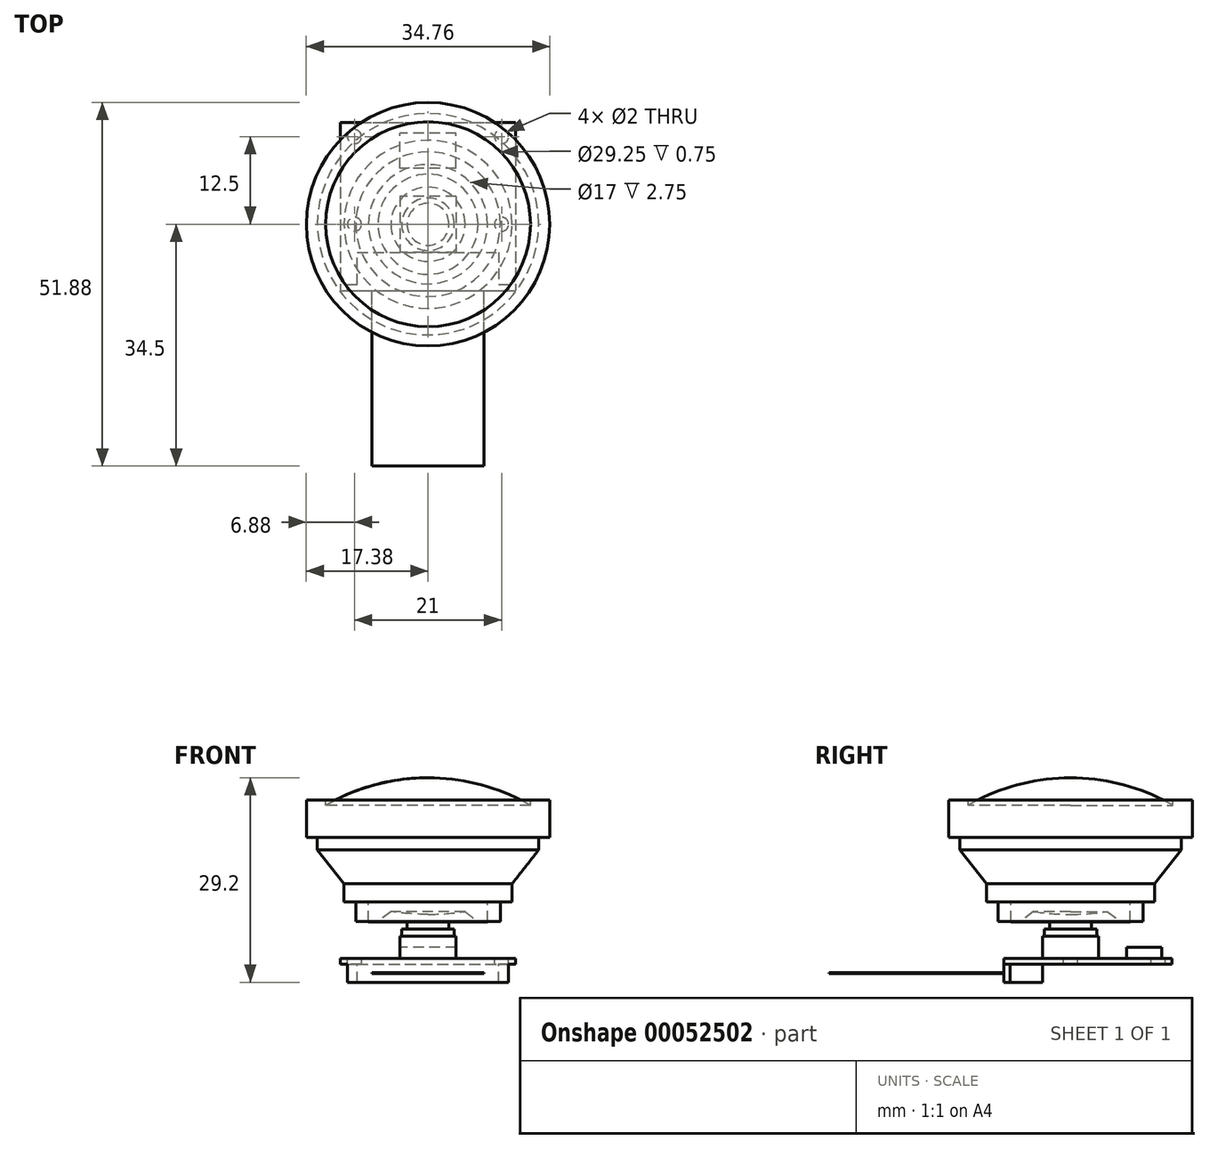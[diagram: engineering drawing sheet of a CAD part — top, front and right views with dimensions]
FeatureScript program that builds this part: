
annotation { "Feature Type Name" : "Feature", "Feature Type Description" : "" }
export const myFeature = defineFeature(function(context is Context, id is Id, definition is map)
    precondition{}
    {
        {
            var Q0;
            Q0=qCreatedBy(makeId("Top.planeOp"),FACE);
            var sketch = newSketch(context, id + "F0", { "sketchPlane" : qUnion([Q0])});
            skLineSegment(sketch, "E0.bottom", {"start": v(-12.5, 14.5) * mm, "end": v(12.5, 14.5) * mm});
            skLineSegment(sketch, "E0.top", {"start": v(-12.5, -9.5) * mm, "end": v(12.5, -9.5) * mm});
            skLineSegment(sketch, "E0.left", {"start": v(-12.5, 14.5) * mm, "end": v(-12.5, -9.5) * mm});
            skLineSegment(sketch, "E0.right", {"start": v(12.5, 14.5) * mm, "end": v(12.5, -9.5) * mm});
            skSolve(sketch);
        }
        {
            var Q0;
            Q0=qSketchRegion(id+"F0",true);
            extrude(context, id + "F1", {"entities" : qUnion([Q0]), "oppositeDirection" : true, "depth" : .8 * mm});
        }
        {
            var Q0;
            Q0=makeQuery(id+"F1.opExtrude","CAP_FACE",FACE,{"disambiguationData":[OSD([sQuery(id+"F0.wireOp",EDGE,"E0.bottom"),sQuery(id+"F0.wireOp",EDGE,"E0.top"),sQuery(id+"F0.wireOp",EDGE,"E0.left"),sQuery(id+"F0.wireOp",EDGE,"E0.right")])],"isStart":true});
            var sketch = newSketch(context, id + "F2", { "sketchPlane" : qUnion([Q0])});
            skLineSegment(sketch, "E1.rect.bottom", {"start": v(4, 4) * mm, "end": v(-4, 4) * mm});
            skLineSegment(sketch, "E1.rect.top", {"start": v(4, -4) * mm, "end": v(-4, -4) * mm});
            skLineSegment(sketch, "E1.rect.left", {"start": v(4, 4) * mm, "end": v(4, -4) * mm});
            skLineSegment(sketch, "E1.rect.right", {"start": v(-4, 4) * mm, "end": v(-4, -4) * mm});
            skPoint(sketch, "E1.rect.middle", {"position": v(0, 0) * mm});
            skSolve(sketch);
        }
        {
            var Q0;
            Q0=qSketchRegion(id+"F2",true);
            extrude(context, id + "F3", {"entities" : qUnion([Q0]), "operationType" : NewBodyOperationType.ADD, "depth" : 3.2 * mm});
        }
        {
            var Q0;
            Q0=makeQuery(id+"F3.opExtrude","CAP_FACE",FACE,{"disambiguationData":[OSD([sQuery(id+"F2.wireOp",EDGE,"E1.rect.bottom"),sQuery(id+"F2.wireOp",EDGE,"E1.rect.top"),sQuery(id+"F2.wireOp",EDGE,"E1.rect.left"),sQuery(id+"F2.wireOp",EDGE,"E1.rect.right")])],"isStart":false});
            var sketch = newSketch(context, id + "F4", { "sketchPlane" : qUnion([Q0])});
            skCircle(sketch, "E2", {"center": v(0, 0) * mm, "radius": 3.75 * mm});
            skSolve(sketch);
        }
        {
            var Q0;
            Q0=qSketchRegion(id+"F4",true);
            var Q1;
            Q1=sQuery(id+"F4.wireOp",EDGE,"E2");
            extrude(context, id + "F5", {"entities" : qUnion([Q0]), "operationType" : NewBodyOperationType.ADD, "surfaceEntities" : qUnion([Q1]), "depth" : 1 * mm});
        }
        {
            var Q0;
            Q0=makeQuery(id+"F5.opExtrude","CAP_FACE",FACE,{"disambiguationData":[OSD([sQuery(id+"F4.wireOp",EDGE,"E2")])],"isStart":false});
            var sketch = newSketch(context, id + "F6", { "sketchPlane" : qUnion([Q0])});
            skCircle(sketch, "E3", {"center": v(0, 0) * mm, "radius": 3 * mm});
            skSolve(sketch);
        }
        {
            var Q0;
            Q0=qSketchRegion(id+"F6",true);
            extrude(context, id + "F7", {"entities" : qUnion([Q0]), "operationType" : NewBodyOperationType.ADD, "depth" : 1 * mm});
        }
        {
            var Q0;
            Q0=makeQuery(id+"F1.opExtrude","CAP_FACE",FACE,{"disambiguationData":[OSD([sQuery(id+"F0.wireOp",EDGE,"E0.bottom"),sQuery(id+"F0.wireOp",EDGE,"E0.top"),sQuery(id+"F0.wireOp",EDGE,"E0.left"),sQuery(id+"F0.wireOp",EDGE,"E0.right")])],"isStart":true});
            var sketch = newSketch(context, id + "F8", { "sketchPlane" : qUnion([Q0])});
            skPoint(sketch, "E4", {"position": v(-10.5, 12.5) * mm});
            skPoint(sketch, "E5", {"position": v(10.5, 12.5) * mm});
            skPoint(sketch, "E6", {"position": v(10.5, 0) * mm});
            skPoint(sketch, "E7", {"position": v(-10.5, 0) * mm});
            skSolve(sketch);
        }
        {
            var Q0;
            Q0=makeQuery(id+"F1.opExtrude","CAP_FACE",FACE,{"disambiguationData":[OSD([sQuery(id+"F0.wireOp",EDGE,"E0.bottom"),sQuery(id+"F0.wireOp",EDGE,"E0.top"),sQuery(id+"F0.wireOp",EDGE,"E0.left"),sQuery(id+"F0.wireOp",EDGE,"E0.right")])],"isStart":true});
            var sketch = newSketch(context, id + "F9", { "sketchPlane" : qUnion([Q0])});
            skLineSegment(sketch, "E8.bottom", {"start": v(4, 8) * mm, "end": v(-4, 8) * mm});
            skLineSegment(sketch, "E8.top", {"start": v(4, 13) * mm, "end": v(-4, 13) * mm});
            skLineSegment(sketch, "E8.left", {"start": v(4, 8) * mm, "end": v(4, 13) * mm});
            skLineSegment(sketch, "E8.right", {"start": v(-4, 8) * mm, "end": v(-4, 13) * mm});
            skSolve(sketch);
        }
        {
            var Q0;
            Q0=qSketchRegion(id+"F9",true);
            extrude(context, id + "F10", {"entities" : qUnion([Q0]), "operationType" : NewBodyOperationType.ADD, "depth" : 1.6 * mm});
        }
        {
            var Q0;
            Q0=makeQuery(id+"F1.opExtrude","CAP_FACE",FACE,{"disambiguationData":[OSD([sQuery(id+"F0.wireOp",EDGE,"E0.bottom"),sQuery(id+"F0.wireOp",EDGE,"E0.top"),sQuery(id+"F0.wireOp",EDGE,"E0.left"),sQuery(id+"F0.wireOp",EDGE,"E0.right")])],"isStart":false});
            var sketch = newSketch(context, id + "F11", { "sketchPlane" : qUnion([Q0])});
            skLineSegment(sketch, "E9", {"start": v(-11.5, 9.5) * mm, "end": v(-11.5, 8.6) * mm});
            skLineSegment(sketch, "E10", {"start": v(-11.5, 8.6) * mm, "end": v(-10.1, 8.6) * mm});
            skLineSegment(sketch, "E11", {"start": v(-10.1, 8.6) * mm, "end": v(-10.1, 4) * mm});
            skLineSegment(sketch, "E12", {"start": v(-10.1, 4) * mm, "end": v(10.1, 4) * mm});
            skLineSegment(sketch, "E13", {"start": v(10.1, 4) * mm, "end": v(10.1, 8.6) * mm});
            skLineSegment(sketch, "E14", {"start": v(10.1, 8.6) * mm, "end": v(11.5, 8.6) * mm});
            skLineSegment(sketch, "E15", {"start": v(11.5, 8.6) * mm, "end": v(11.5, 9.5) * mm});
            skLineSegment(sketch, "E16", {"start": v(11.5, 9.5) * mm, "end": v(-11.5, 9.5) * mm});
            skSolve(sketch);
        }
        {
            var Q0;
            Q0=qSketchRegion(id+"F11",true);
            extrude(context, id + "F12", {"entities" : qUnion([Q0]), "operationType" : NewBodyOperationType.ADD, "depth" : 2.6 * mm});
        }
        {
            var Q0;
            Q0=makeQuery(id+"F12.boolean.opBoolean","MERGE",FACE,{"derivedFrom":[makeQuery(id+"F1.opExtrude","SWEPT_FACE",FACE,{"disambiguationData":[OSD([sQuery(id+"F0.wireOp",EDGE,"E0.top")])]}),makeQuery(id+"F12.opExtrude","SWEPT_FACE",FACE,{"disambiguationData":[OSD([sQuery(id+"F11.wireOp",EDGE,"E16")])]})]});
            var sketch = newSketch(context, id + "F13", { "sketchPlane" : qUnion([Q0])});
            skLineSegment(sketch, "E17.bottom", {"start": v(-8, -2) * mm, "end": v(8, -2) * mm});
            skLineSegment(sketch, "E17.top", {"start": v(-8, -2.15) * mm, "end": v(8, -2.15) * mm});
            skLineSegment(sketch, "E17.left", {"start": v(-8, -2) * mm, "end": v(-8, -2.15) * mm});
            skLineSegment(sketch, "E17.right", {"start": v(8, -2) * mm, "end": v(8, -2.15) * mm});
            skSolve(sketch);
        }
        {
            var Q0;
            Q0=qSketchRegion(id+"F13",true);
            extrude(context, id + "F14", {"entities" : qUnion([Q0]), "operationType" : NewBodyOperationType.ADD, "depth" : 25 * mm});
        }
        {
            var Q0;
            Q0=sQuery(id+"F8.wireOp",VERTEX,"E4");
            var Q1;
            Q1=sQuery(id+"F8.wireOp",VERTEX,"E5");
            var Q2;
            Q2=sQuery(id+"F8.wireOp",VERTEX,"E7");
            var Q3;
            Q3=sQuery(id+"F8.wireOp",VERTEX,"E6");
            var Q4;
            Q4=makeQuery(id+"F1.opExtrude","SWEPT_BODY",BODY,{"disambiguationData":[OSD([sQuery(id+"F0.wireOp",EDGE,"E0.bottom"),sQuery(id+"F0.wireOp",EDGE,"E0.top"),sQuery(id+"F0.wireOp",EDGE,"E0.left"),sQuery(id+"F0.wireOp",EDGE,"E0.right")])]});
            hole(context, id + "F15", {"style" : HoleStyle.SIMPLE, "holeDiameter" : 2 * mm, "endStyle" : HoleEndStyle.THROUGH, "locations" : qUnion([Q0, Q1, Q2, Q3]), "scope" : qUnion([Q4])});
        }
        {
            var Q0;
            Q0=qCreatedBy(makeId("Front.planeOp"),FACE);
            var sketch = newSketch(context, id + "F16", { "sketchPlane" : qUnion([Q0])});
            skLineSegment(sketch, "E18", {"start": v(-8.5, 5.2) * mm, "end": v(-8.5, 8.05) * mm});
            skLineSegment(sketch, "E19", {"start": v(-8.5, 8.05) * mm, "end": v(-12, 8.05) * mm});
            skLineSegment(sketch, "E20", {"start": v(-12, 8.05) * mm, "end": v(-12, 10.65) * mm});
            skLineSegment(sketch, "E21", {"start": v(-12, 10.65) * mm, "end": v(-15.8, 15.5) * mm});
            skLineSegment(sketch, "E22", {"start": v(-15.8, 15.5) * mm, "end": v(-15.8, 17.25) * mm});
            skLineSegment(sketch, "E23", {"start": v(-15.8, 17.25) * mm, "end": v(-17.38, 17.25) * mm});
            skLineSegment(sketch, "E24", {"start": v(-17.38, 17.25) * mm, "end": v(-17.38, 22.6) * mm});
            skLineSegment(sketch, "E25", {"start": v(-17.38, 22.6) * mm, "end": v(-14.63, 22.6) * mm});
            skLineSegment(sketch, "E26", {"start": v(-14.63, 22.6) * mm, "end": v(-14.63, 21.85) * mm});
            skArc(sketch, "E27", {"start": v(0, 25.8) * mm, "mid": v(-7.57, 24.8) * mm, "end": v(-14.62, 21.85) * mm});
            skLineSegment(sketch, "E28", {"start": v(0, 25.8) * mm, "end": v(0, 5.2) * mm});
            skLineSegment(sketch, "E29", {"start": v(0, 37.32) * mm, "end": v(0, -12.53) * mm, "construction": true});
            skLineSegment(sketch, "E30", {"start": v(-8.5, 5.2) * mm, "end": v(-7.15, 5.2) * mm});
            skLineSegment(sketch, "E31", {"start": v(-7.15, 5.2) * mm, "end": v(-5.3, 6.7) * mm});
            skArc(sketch, "E32", {"start": v(-5.3, 6.7) * mm, "mid": v(-2.66, 6.4) * mm, "end": v(0, 6.3) * mm});
            skSolve(sketch);
        }
        {
            var Q0;
            Q0 = qSketchRegion(id + "F16", true);
            var Q1;
            Q1=sQuery(id+"F16.wireOp",EDGE,"E29");
            revolve(context, id + "F17", {"entities" : qUnion([Q0]), "axis" : qUnion([Q1]), "revolveType" : RevolveType.FULL});
        }
        {
            var Q0;
            Q0=makeQuery(id+"F17.opRevolve","SWEPT_FACE",FACE,{"disambiguationData":[OSD([sQuery(id+"F16.wireOp",EDGE,"E19")])]});
            var sketch = newSketch(context, id + "F18", { "sketchPlane" : qUnion([Q0])});
            skCircle(sketch, "E33", {"center": v(0, 0) * mm, "radius": 8 * mm});
            skCircle(sketch, "E34", {"center": v(0, 0) * mm, "radius": 10.32 * mm});
            skSolve(sketch);
        }
        {
            var Q0;
            Q0=makeQuery(id+"F18.imprint","IMPRINT",FACE,{"disambiguationData":[TD([[makeQuery(id+"F18.imprint","IMPRINT",EDGE,{"derivedFrom":sQuery(id+"F18.wireOp",EDGE,"E34")}),1.0]])]});
            extrude(context, id + "F19", {"entities" : qUnion([Q0]), "depth" : 2.75 * mm});
        }
    });
